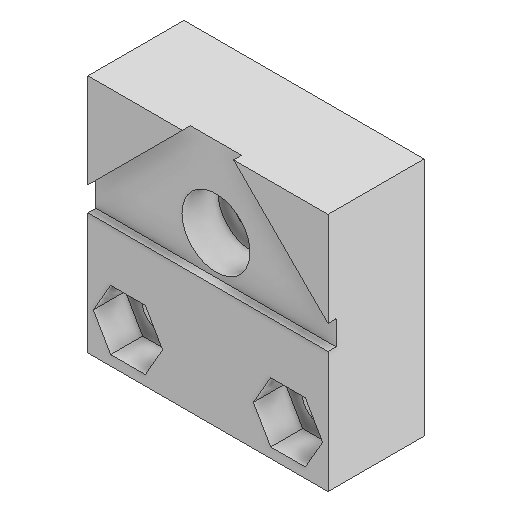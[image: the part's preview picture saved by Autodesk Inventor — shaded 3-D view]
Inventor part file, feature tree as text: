
AUTODESK INVENTOR PART (.ipt)
format: ipt  version: 2022 (Build 260153000, 153)  size: 192,512 bytes
history: native  units: mm
features: extrude x6, sketch x4
ambient origin geometry x8: Origin, YZ Plane, XZ Plane, XY Plane, X Axis, Y Axis, Z Axis, Center Point
bodies: Solid1 (feature_tree)
feature tree (10):
  extrude  "Extrusion1"  Depth=30.0mm
  extrude  "Extrusion2"  Depth=15.0mm
  extrude  "Extrusion3"  Depth=12.0mm TaperAngle=0.0deg
  extrude  "Extrusion4"  Depth=10.0mm
  extrude  "Extrusion5"  Depth=10.0mm
  extrude  "Extrusion6"  TaperAngle=45.0deg  [1 undecoded]
  sketch  "Sketch1"  dims[d0=30.0mm d1=30.0mm]
  sketch  "Sketch4"  dims[d2=15.0mm d3=15.0mm]
  sketch  "Sketch5"  dims[d4=12.0mm d5=0.0mm d7=12.0mm d8=0.0mm]
  sketch  "Sketch6"  dims[d10=5.5mm d11=0.0mm d12=18.2mm d13=25.5mm d14=45.0deg d16=1.0mm d17=0.0mm d18=4.5mm d19=5.0mm d20=5.0mm d21=4.5mm d22=5.0mm d23=5.0mm d24=12.0mm d25=0.0mm d26=25.5mm d27=45.0deg d28=7.5mm d29=7.5mm d30=4.0mm d31=0.0mm d32=8.5mm d33=10.0mm d34=4.5mm d35=10.0mm]
note: 1 required parameter value undecoded (feature->parameter linkage not recoverable at this tier; creation-order binding heuristic only, values carry confidence <= 0.55)
